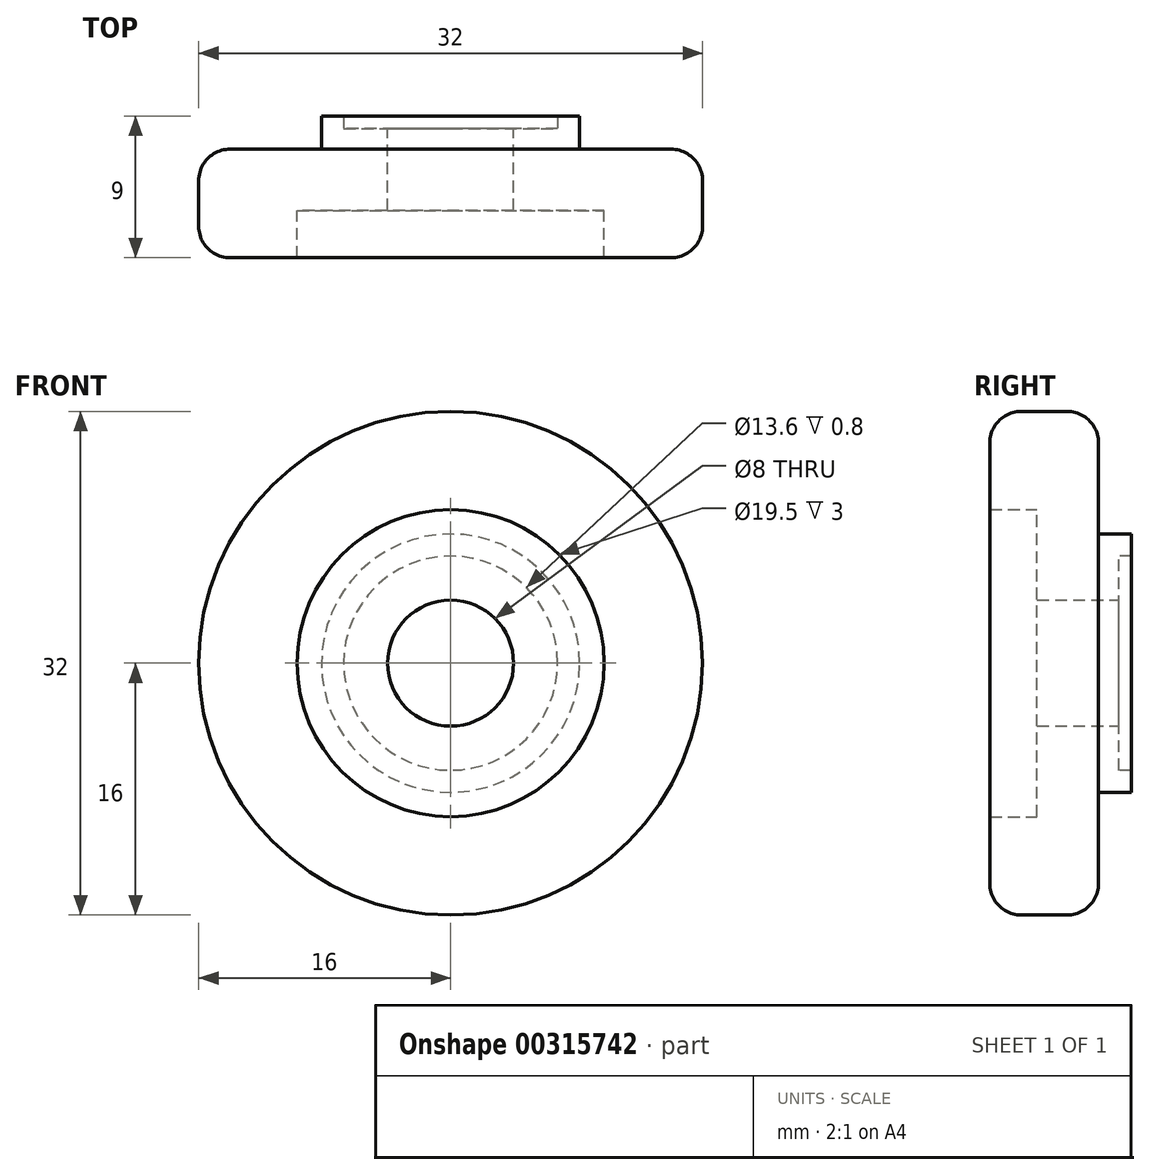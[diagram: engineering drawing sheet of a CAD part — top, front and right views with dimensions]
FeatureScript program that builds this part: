
annotation { "Feature Type Name" : "Feature", "Feature Type Description" : "" }
export const myFeature = defineFeature(function(context is Context, id is Id, definition is map)
    precondition{}
    {
        {
            var Q0;
            Q0=qCreatedBy(makeId("Front.planeOp"),FACE);
            var sketch = newSketch(context, id + "F0", { "sketchPlane" : qUnion([Q0])});
            skCircle(sketch, "E0", {"center": v(0, 0) * mm, "radius": 4 * mm});
            skCircle(sketch, "E1", {"center": v(0, 0) * mm, "radius": 9.75 * mm});
            skCircle(sketch, "E2", {"center": v(0, 0) * mm, "radius": 16 * mm});
            skSolve(sketch);
        }
        {
            var Q0;
            Q0=makeQuery(id+"F0.imprint","IMPRINT",FACE,{"disambiguationData":[TD([[makeQuery(id+"F0.imprint","IMPRINT",EDGE,{"derivedFrom":sQuery(id+"F0.wireOp",EDGE,"E0")}),-1.0]])]});
            extrude(context, id + "F1", {"entities" : qUnion([Q0]), "depth" : 3.9 * mm});
        }
        {
            var Q0;
            Q0=makeQuery(id+"F0.imprint","IMPRINT",FACE,{"disambiguationData":[TD([[makeQuery(id+"F0.imprint","IMPRINT",EDGE,{"derivedFrom":sQuery(id+"F0.wireOp",EDGE,"E1")}),-1.0]])]});
            extrude(context, id + "F2", {"entities" : qUnion([Q0]), "operationType" : NewBodyOperationType.ADD, "depth" : 6.9 * mm});
        }
        {
            var Q0;
            Q0=qCreatedBy(makeId("Front.planeOp"),FACE);
            var sketch = newSketch(context, id + "F3", { "sketchPlane" : qUnion([Q0])});
            skCircle(sketch, "E3", {"center": v(0, 0) * mm, "radius": 8.2 * mm});
            skCircle(sketch, "E4", {"center": v(0, 0) * mm, "radius": 6.8 * mm});
            skCircle(sketch, "E5", {"center": v(0, 0) * mm, "radius": 4 * mm});
            skSolve(sketch);
        }
        {
            var Q0;
            Q0=makeQuery(id+"F3.imprint","IMPRINT",FACE,{"disambiguationData":[TD([[makeQuery(id+"F3.imprint","IMPRINT",EDGE,{"derivedFrom":sQuery(id+"F3.wireOp",EDGE,"E3")}),1.0]])]});
            extrude(context, id + "F4", {"entities" : qUnion([Q0]), "operationType" : NewBodyOperationType.ADD, "oppositeDirection" : true, "depth" : 2.1 * mm});
        }
        {
            var Q0;
            Q0=makeQuery(id+"F3.imprint","IMPRINT",FACE,{"disambiguationData":[TD([[makeQuery(id+"F3.imprint","IMPRINT",EDGE,{"derivedFrom":sQuery(id+"F3.wireOp",EDGE,"E4")}),1.0]])]});
            extrude(context, id + "F5", {"entities" : qUnion([Q0]), "operationType" : NewBodyOperationType.ADD, "oppositeDirection" : true, "depth" : 1.3 * mm});
        }
        {
            var Q0;
            Q0=makeQuery(id+"F2.opExtrude","CAP_EDGE",EDGE,{"disambiguationData":[OSD([sQuery(id+"F0.wireOp",EDGE,"E2")])],"isStart":false});
            var Q1;
            Q1=makeQuery(id+"F2.opExtrude","CAP_EDGE",EDGE,{"disambiguationData":[OSD([sQuery(id+"F0.wireOp",EDGE,"E2")])],"isStart":true});
            fillet(context, id + "F6", {"entities" : qUnion([Q0, Q1]), "radius" : 2 * mm, "tangentPropagation" : true, "allowEdgeOverflow" : false});
        }
    });
